# Revit family: CHI_Overhead_MaxRoll_MR6850
name_source: partatom
category: Doors
units: mm (PartAtom-declared; Revit-internal decimal feet)

## family parameters
Always vertical = Yes
Classification Number = 23.30.10.00
Cut with Voids When Loaded = No
Host = Wall
Room Calculation Point = No
Shared = No

## types (7) — shared parameters
Construction Details = https://www.arcat.com
Frame Projection Ext. = 0' - 1"
Frame Projection Int. = 0' - 1"
Frame Width = 0' - 3"
Function = Interior
Installation-Fabrication = https://performaxglobal.com
Manufacturer = C.H.I. Overhead Doors
Manufacturer Fax = 217-543-4454
Manufacturer Website = https://www.chiohd.com
Product Data = https://performaxglobal.com
Sales Information = https://performaxglobal.com
Specification = https://www.arcat.com
URL = https://performaxglobal.com
Wall Closure = By host

## per-type parameters (varying)
| type | Chain Length | Head Height | Height | Model | Overall Height | Overall Width | Width |
| 10'W x 10'H | 7' - 0" | 1' - 5" | 10' - 0" | MaxRoll MR6850 120x120 | 11' - 3" | 10' - 10" | 10' - 0" |
| 6'W x 6'H | 3' - 0" | 1' - 5" | 6' - 0" | MaxRoll MR6850 72x72 | 7' - 3" | 6' - 10" | 6' - 0" |
| 8'W x 8'H | 5' - 0" | 1' - 5" | 8' - 0" | MaxRoll MR6850 96x92 | 9' - 3" | 8' - 10" | 8' - 0" |
| 12'W x 12'H | 9' - 0" | 1' - 5" | 12' - 0" | MaxRoll MR6850 144x144 | 13' - 3" | 12' - 10" | 12' - 0" |
| 14'W x 14'H | 11' - 0" | 1' - 8" | 14' - 0" | MaxRoll MR6850 168x168 | 15' - 3" | 14' - 10" | 14' - 0" |
| 16'W x 16'H | 13' - 0" | 1' - 8" | 16' - 0" | MaxRoll MR6850 192x192 | 17' - 3" | 16' - 10" | 16' - 0" |
| 18'W x 18'H | 15' - 0" | 1' - 8" | 18' - 0" | MaxRoll MR6850 216x216 | 19' - 3" | 18' - 10" | 18' - 0" |

## geometry (parser evidence)
native form markers: Sweep x9
no freeform markers — native parametric forms only
